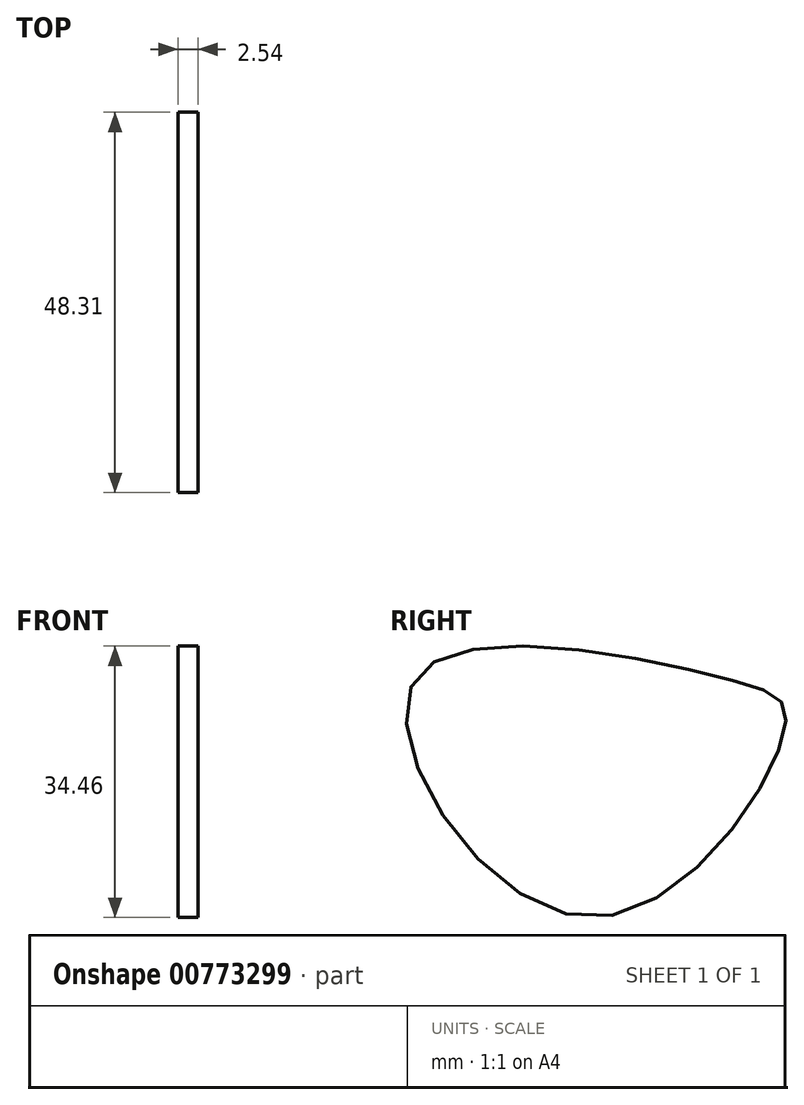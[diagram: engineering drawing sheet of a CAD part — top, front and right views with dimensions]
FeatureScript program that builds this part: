
annotation { "Feature Type Name" : "Feature", "Feature Type Description" : "" }
export const myFeature = defineFeature(function(context is Context, id is Id, definition is map)
    precondition{}
    {
        {
            var Q0;
            Q0=qCreatedBy(makeId("Front.planeOp"),FACE);
            var sketch = newSketch(context, id + "F0", { "sketchPlane" : qUnion([Q0])});
            skCircle(sketch, "E0.cCircle", {"center": v(0, 0) * mm, "radius": 46.36 * mm, "construction": true});
            skLineSegment(sketch, "E0.0", {"start": v(46.36, 0) * mm, "end": v(39, -25.07) * mm});
            skLineSegment(sketch, "E0.1", {"start": v(39, -25.07) * mm, "end": v(19.26, -42.17) * mm});
            skLineSegment(sketch, "E0.2", {"start": v(19.26, -42.17) * mm, "end": v(-6.6, -45.9) * mm});
            skLineSegment(sketch, "E0.3", {"start": v(-6.6, -45.9) * mm, "end": v(-30.36, -35.04) * mm});
            skLineSegment(sketch, "E0.4", {"start": v(-30.36, -35.04) * mm, "end": v(-44.49, -13.06) * mm});
            skLineSegment(sketch, "E0.5", {"start": v(-44.49, -13.06) * mm, "end": v(-44.49, 13.06) * mm});
            skLineSegment(sketch, "E0.6", {"start": v(-44.49, 13.06) * mm, "end": v(-30.36, 35.04) * mm});
            skLineSegment(sketch, "E0.7", {"start": v(-30.36, 35.04) * mm, "end": v(-6.6, 45.9) * mm});
            skLineSegment(sketch, "E0.8", {"start": v(-6.6, 45.9) * mm, "end": v(19.26, 42.17) * mm});
            skLineSegment(sketch, "E0.9", {"start": v(19.26, 42.17) * mm, "end": v(39, 25.07) * mm});
            skLineSegment(sketch, "E0.10", {"start": v(39, 25.07) * mm, "end": v(46.36, 0) * mm});
            skSolve(sketch);
        }
        {
            var Q0;
            Q0=makeQuery(id+"F0.imprint","IMPRINT",FACE,{"disambiguationData":[TD([[makeQuery(id+"F0.imprint","IMPRINT",EDGE,{"derivedFrom":sQuery(id+"F0.wireOp",EDGE,"E0.0")}),-1.0]])]});
            extrude(context, id + "F1", {"entities" : qUnion([Q0]), "depth" : 2.54 * mm, "offsetDistance" : 25.4 * mm});
        }
        {
            var Q0;
            Q0=makeQuery(id+"F1.opExtrude","SWEPT_BODY",BODY,{"disambiguationData":[OSD([sQuery(id+"F0.wireOp",EDGE,"E0.0"),sQuery(id+"F0.wireOp",EDGE,"E0.1"),sQuery(id+"F0.wireOp",EDGE,"E0.2"),sQuery(id+"F0.wireOp",EDGE,"E0.3"),sQuery(id+"F0.wireOp",EDGE,"E0.4"),sQuery(id+"F0.wireOp",EDGE,"E0.5"),sQuery(id+"F0.wireOp",EDGE,"E0.6"),sQuery(id+"F0.wireOp",EDGE,"E0.7"),sQuery(id+"F0.wireOp",EDGE,"E0.8"),sQuery(id+"F0.wireOp",EDGE,"E0.9"),sQuery(id+"F0.wireOp",EDGE,"E0.10")])]});
            deleteBodies(context, id + "F2", {"entities" : qUnion([Q0])});
        }
        {
            var Q0;
            Q0=qCreatedBy(makeId("Right.planeOp"),FACE);
            var sketch = newSketch(context, id + "F3", { "sketchPlane" : qUnion([Q0])});
            skFitSpline(sketch, "E1", {"points": [v(18.83, -13.29) * mm, v(-21.75, -13.58) * mm, v(0, -43.36) * mm, v(25.55, -19.13) * mm, v(18.83, -13.29) * mm]});
            skSolve(sketch);
        }
        {
            var Q0;
            Q0 = qSketchRegion(id + "F3", true);
            extrude(context, id + "F4", {"entities" : qUnion([Q0]), "oppositeDirection" : true, "depth" : 2.54 * mm, "offsetDistance" : 25.4 * mm});
        }
    });
